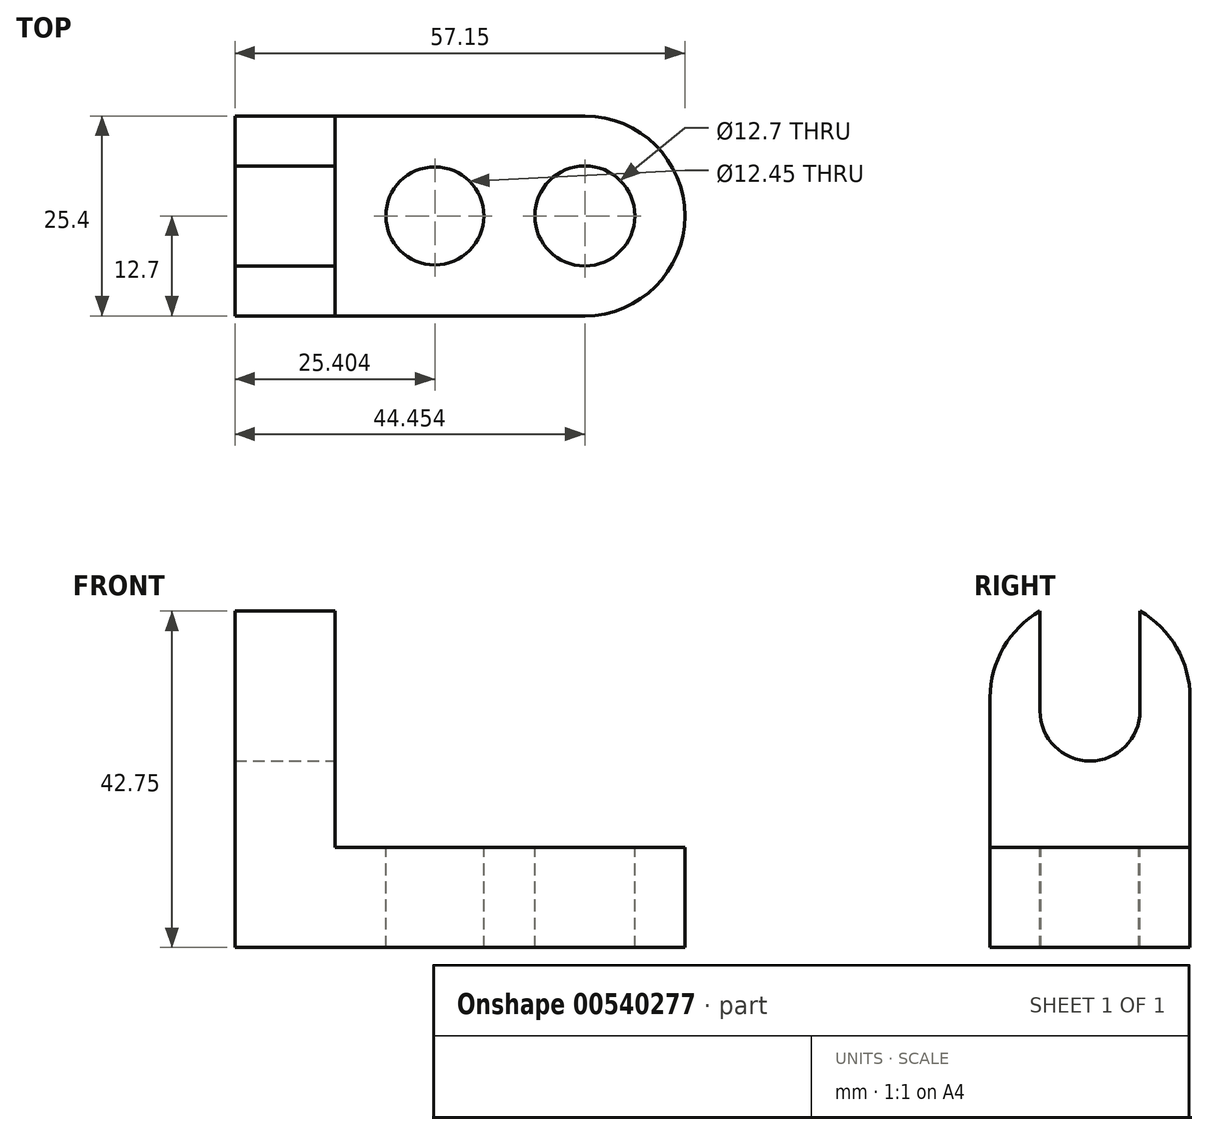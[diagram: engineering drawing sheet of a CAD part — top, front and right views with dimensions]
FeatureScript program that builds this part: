
annotation { "Feature Type Name" : "Feature", "Feature Type Description" : "" }
export const myFeature = defineFeature(function(context is Context, id is Id, definition is map)
    precondition{}
    {
        {
            var Q0;
            Q0=qCreatedBy(makeId("Front.planeOp"),FACE);
            var sketch = newSketch(context, id + "F0", { "sketchPlane" : qUnion([Q0])});
            skLineSegment(sketch, "E0", {"start": v(-31, 44.45) * mm, "end": v(-31, 0) * mm});
            skLineSegment(sketch, "E1", {"start": v(-31, 0) * mm, "end": v(26.14, 0) * mm});
            skLineSegment(sketch, "E2", {"start": v(26.14, 0) * mm, "end": v(26.14, 12.7) * mm});
            skLineSegment(sketch, "E3", {"start": v(26.14, 12.7) * mm, "end": v(-18.3, 12.7) * mm});
            skLineSegment(sketch, "E4", {"start": v(-18.3, 12.7) * mm, "end": v(-18.3, 44.45) * mm});
            skLineSegment(sketch, "E5", {"start": v(-18.3, 44.45) * mm, "end": v(-31, 44.45) * mm});
            skSolve(sketch);
        }
        {
            var Q0;
            Q0=makeQuery(id+"F0.imprint","IMPRINT",FACE,{"disambiguationData":[TD([[makeQuery(id+"F0.imprint","IMPRINT",EDGE,{"derivedFrom":sQuery(id+"F0.wireOp",EDGE,"E0")}),1.0]])]});
            extrude(context, id + "F1", {"entities" : qUnion([Q0]), "depth" : 25.4 * mm, "offsetDistance" : 25.4 * mm});
        }
        {
            var Q0;
            Q0=makeQuery(id+"F1.opExtrude","SWEPT_FACE",FACE,{"disambiguationData":[OSD([sQuery(id+"F0.wireOp",EDGE,"E3")])]});
            var sketch = newSketch(context, id + "F2", { "sketchPlane" : qUnion([Q0])});
            skCircle(sketch, "E6", {"center": v(-5.6, -12.7) * mm, "radius": 6.22 * mm});
            skCircle(sketch, "E7", {"center": v(13.44, -12.7) * mm, "radius": 6.35 * mm});
            skSolve(sketch);
        }
        {
            var Q0;
            Q0 = qSketchRegion(id + "F2", true);
            var Q1;
            Q1 = qSketchRegion(id + "FySjiP1aUgdDXVq_1", true);
            extrude(context, id + "F3", {"entities" : qUnion([Q0, Q1]), "operationType" : NewBodyOperationType.REMOVE, "endBound" : BoundingType.THROUGH_ALL, "oppositeDirection" : true, "depth" : 25.4 * mm, "offsetDistance" : 25.4 * mm});
        }
        {
            var Q0;
            Q0=makeQuery(id+"F1.opExtrude","SWEPT_FACE",FACE,{"disambiguationData":[OSD([sQuery(id+"F0.wireOp",EDGE,"E3")])]});
            var sketch = newSketch(context, id + "F4", { "sketchPlane" : qUnion([Q0])});
            skArc(sketch, "E8", {"start": v(13.44, -25.4) * mm, "mid": v(26.14, -12.7) * mm, "end": v(13.44, 0) * mm});
            skSolve(sketch);
        }
        {
            var Q0;
            Q0=makeQuery(id+"F4.imprint","IMPRINT",FACE,{"disambiguationData":[TD([[makeQuery(id+"F4.imprint","IMPRINT",EDGE,{"derivedFrom":makeQuery(id+"F3.boolean.opBoolean","COPY",EDGE,{"derivedFrom":makeQuery(id+"F3.opExtrude","CAP_EDGE",EDGE,{"disambiguationData":[OSD([sQuery(id+"F2.wireOp",EDGE,"E6")])],"isStart":true})})}),-1.0]])]});
            var sketch = newSketch(context, id + "F5", { "sketchPlane" : qUnion([Q0])});
            skArc(sketch, "E9", {"start": v(16.25, -25.1) * mm, "mid": v(26.34, -12.68) * mm, "end": v(16.6, 0) * mm});
            skSolve(sketch);
        }
        {
            var Q0;
            {var subQ0=sQuery(id+"F4.wireOp",EDGE,"E8");var subQ1=sQuery(id+"F0.wireOp",EDGE,"E3");var subQ2=makeQuery(id+"F1.opExtrude","CAP_EDGE",EDGE,{"disambiguationData":[OSD([subQ1])],"isStart":true});var subQ3=makeQuery(id+"F4.imprint","INTERSECT",VERTEX,{"derivedFrom":[subQ2,subQ0]});Q0=makeQuery(id+"F4.imprint","IMPRINT",FACE,{"disambiguationData":[TD([[makeQuery(id+"F4.imprint","IMPRINT",EDGE,{"disambiguationData":[TD([[subQ3,1.0]])],"derivedFrom":subQ0}),-1.0]])]});}
            var Q1;
            {var subQ0=sQuery(id+"F4.wireOp",EDGE,"E8");var subQ1=sQuery(id+"F0.wireOp",EDGE,"E3");var subQ2=makeQuery(id+"F1.opExtrude","CAP_EDGE",EDGE,{"disambiguationData":[OSD([subQ1])],"isStart":false});var subQ3=makeQuery(id+"F4.imprint","INTERSECT",VERTEX,{"derivedFrom":[subQ2,subQ0]});Q1=makeQuery(id+"F4.imprint","IMPRINT",FACE,{"disambiguationData":[TD([[makeQuery(id+"F4.imprint","IMPRINT",EDGE,{"disambiguationData":[TD([[subQ3,-1.0]])],"derivedFrom":subQ0}),-1.0]])]});}
            var Q2;
            Q2 = qConstructionFilter(qBodyType(qCreatedBy(id + "F5" ,EDGE), BodyType.WIRE), ConstructionObject.NO);
            extrude(context, id + "F6", {"entities" : qUnion([Q0, Q1]), "operationType" : NewBodyOperationType.REMOVE, "surfaceEntities" : qUnion([Q2]), "endBound" : BoundingType.THROUGH_ALL, "oppositeDirection" : true, "depth" : 25.4 * mm, "offsetDistance" : 25.4 * mm});
        }
        {
            var Q0;
            Q0=makeQuery(id+"F1.opExtrude","SWEPT_FACE",FACE,{"disambiguationData":[OSD([sQuery(id+"F0.wireOp",EDGE,"E4")])]});
            var sketch = newSketch(context, id + "F7", { "sketchPlane" : qUnion([Q0])});
            skArc(sketch, "E10", {"start": v(0, 31.75) * mm, "mid": v(-12.7, 44.45) * mm, "end": v(-25.4, 31.75) * mm});
            skSolve(sketch);
        }
        {
            var Q0;
            {var subQ0=sQuery(id+"F7.wireOp",EDGE,"E10");var subQ1=sQuery(id+"F0.wireOp",EDGE,"E4");var subQ2=makeQuery(id+"F1.opExtrude","CAP_EDGE",EDGE,{"disambiguationData":[OSD([subQ1])],"isStart":true});var subQ3=makeQuery(id+"F7.imprint","INTERSECT",VERTEX,{"derivedFrom":[subQ2,subQ0]});Q0=makeQuery(id+"F7.imprint","IMPRINT",FACE,{"disambiguationData":[TD([[makeQuery(id+"F7.imprint","IMPRINT",EDGE,{"disambiguationData":[TD([[subQ3,-1.0]])],"derivedFrom":subQ0}),-1.0]])]});}
            var Q1;
            {var subQ0=sQuery(id+"F7.wireOp",EDGE,"E10");var subQ1=sQuery(id+"F0.wireOp",EDGE,"E4");var subQ2=makeQuery(id+"F1.opExtrude","CAP_EDGE",EDGE,{"disambiguationData":[OSD([subQ1])],"isStart":false});var subQ3=makeQuery(id+"F7.imprint","INTERSECT",VERTEX,{"derivedFrom":[subQ2,subQ0]});Q1=makeQuery(id+"F7.imprint","IMPRINT",FACE,{"disambiguationData":[TD([[makeQuery(id+"F7.imprint","IMPRINT",EDGE,{"disambiguationData":[TD([[subQ3,1.0]])],"derivedFrom":subQ0}),-1.0]])]});}
            var Q2;
            Q2=sQuery(id+"F7.wireOp",EDGE,"E10");
            extrude(context, id + "F8", {"entities" : qUnion([Q0, Q1]), "operationType" : NewBodyOperationType.REMOVE, "surfaceEntities" : qUnion([Q2]), "endBound" : BoundingType.THROUGH_ALL, "oppositeDirection" : true, "depth" : 25.4 * mm, "offsetDistance" : 25.4 * mm});
        }
        {
            var Q0;
            {var subQ0=sQuery(id+"F0.wireOp",EDGE,"E4");var subQ1=makeQuery(id+"F1.opExtrude","SWEPT_EDGE",EDGE,{"disambiguationData":[OSD([sQuery(id+"F0.wireOp",EDGE,"E3"),subQ0])]});Q0=makeQuery(id+"F7.imprint","IMPRINT",FACE,{"disambiguationData":[TD([[makeQuery(id+"F7.imprint","IMPRINT",EDGE,{"derivedFrom":subQ1}),1.0]])]});}
            var sketch = newSketch(context, id + "F9", { "sketchPlane" : qUnion([Q0])});
            skLineSegment(sketch, "E11", {"start": v(-19.05, 42.75) * mm, "end": v(-19.05, 30.05) * mm});
            skLineSegment(sketch, "E12", {"start": v(-6.35, 42.75) * mm, "end": v(-6.35, 30.05) * mm});
            skArc(sketch, "E13", {"start": v(-19.05, 30.05) * mm, "mid": v(-12.7, 23.7) * mm, "end": v(-6.35, 30.05) * mm});
            skSolve(sketch);
        }
        {
            var Q0;
            Q0 = qSketchRegion(id + "F9", true);
            var Q1;
            {var subQ7=sQuery(id+"F9.wireOp",EDGE,"E11");Q1=makeQuery(id+"F9.imprint","IMPRINT",FACE,{"disambiguationData":[TD([[makeQuery(id+"F9.imprint","IMPRINT",EDGE,{"derivedFrom":subQ7}),1.0]])]});}
            extrude(context, id + "F10", {"entities" : qUnion([Q0, Q1]), "operationType" : NewBodyOperationType.REMOVE, "endBound" : BoundingType.THROUGH_ALL, "oppositeDirection" : true, "depth" : 25.4 * mm, "offsetDistance" : 25.4 * mm});
        }
        {
            var Q0;
            {var subQ0=sQuery(id+"F7.wireOp",EDGE,"E10");var subQ1=sQuery(id+"F0.wireOp",EDGE,"E4");var subQ2=makeQuery(id+"F1.opExtrude","CAP_EDGE",EDGE,{"disambiguationData":[OSD([subQ1])],"isStart":true});var subQ3=makeQuery(id+"F7.imprint","INTERSECT",VERTEX,{"derivedFrom":[subQ2,subQ0]});Q0=makeQuery(id+"F7.imprint","IMPRINT",FACE,{"disambiguationData":[TD([[makeQuery(id+"F7.imprint","IMPRINT",EDGE,{"disambiguationData":[TD([[subQ3,-1.0]])],"derivedFrom":subQ0}),-1.0]])]});}
            extrude(context, id + "F11", {"entities" : qUnion([Q0]), "operationType" : NewBodyOperationType.REMOVE, "endBound" : BoundingType.THROUGH_ALL, "oppositeDirection" : true, "depth" : 25.4 * mm, "offsetDistance" : 25.4 * mm});
        }
        {
            var Q0;
            {var subQ0=sQuery(id+"F7.wireOp",EDGE,"E10");var subQ1=sQuery(id+"F0.wireOp",EDGE,"E4");var subQ2=makeQuery(id+"F1.opExtrude","CAP_EDGE",EDGE,{"disambiguationData":[OSD([subQ1])],"isStart":false});var subQ3=makeQuery(id+"F7.imprint","INTERSECT",VERTEX,{"derivedFrom":[subQ2,subQ0]});Q0=makeQuery(id+"F7.imprint","IMPRINT",FACE,{"disambiguationData":[TD([[makeQuery(id+"F7.imprint","IMPRINT",EDGE,{"disambiguationData":[TD([[subQ3,1.0]])],"derivedFrom":subQ0}),-1.0]])]});}
            var Q1;
            {var subQ0=sQuery(id+"F7.wireOp",EDGE,"E10");var subQ1=sQuery(id+"F0.wireOp",EDGE,"E4");var subQ2=makeQuery(id+"F1.opExtrude","CAP_EDGE",EDGE,{"disambiguationData":[OSD([subQ1])],"isStart":true});var subQ3=makeQuery(id+"F7.imprint","INTERSECT",VERTEX,{"derivedFrom":[subQ2,subQ0]});Q1=makeQuery(id+"F7.imprint","IMPRINT",FACE,{"disambiguationData":[TD([[makeQuery(id+"F7.imprint","IMPRINT",EDGE,{"disambiguationData":[TD([[subQ3,-1.0]])],"derivedFrom":subQ0}),-1.0]])]});}
            extrude(context, id + "F12", {"entities" : qUnion([Q0, Q1]), "operationType" : NewBodyOperationType.REMOVE, "endBound" : BoundingType.THROUGH_ALL, "oppositeDirection" : true, "depth" : 25.4 * mm, "offsetDistance" : 25.4 * mm});
        }
    });
